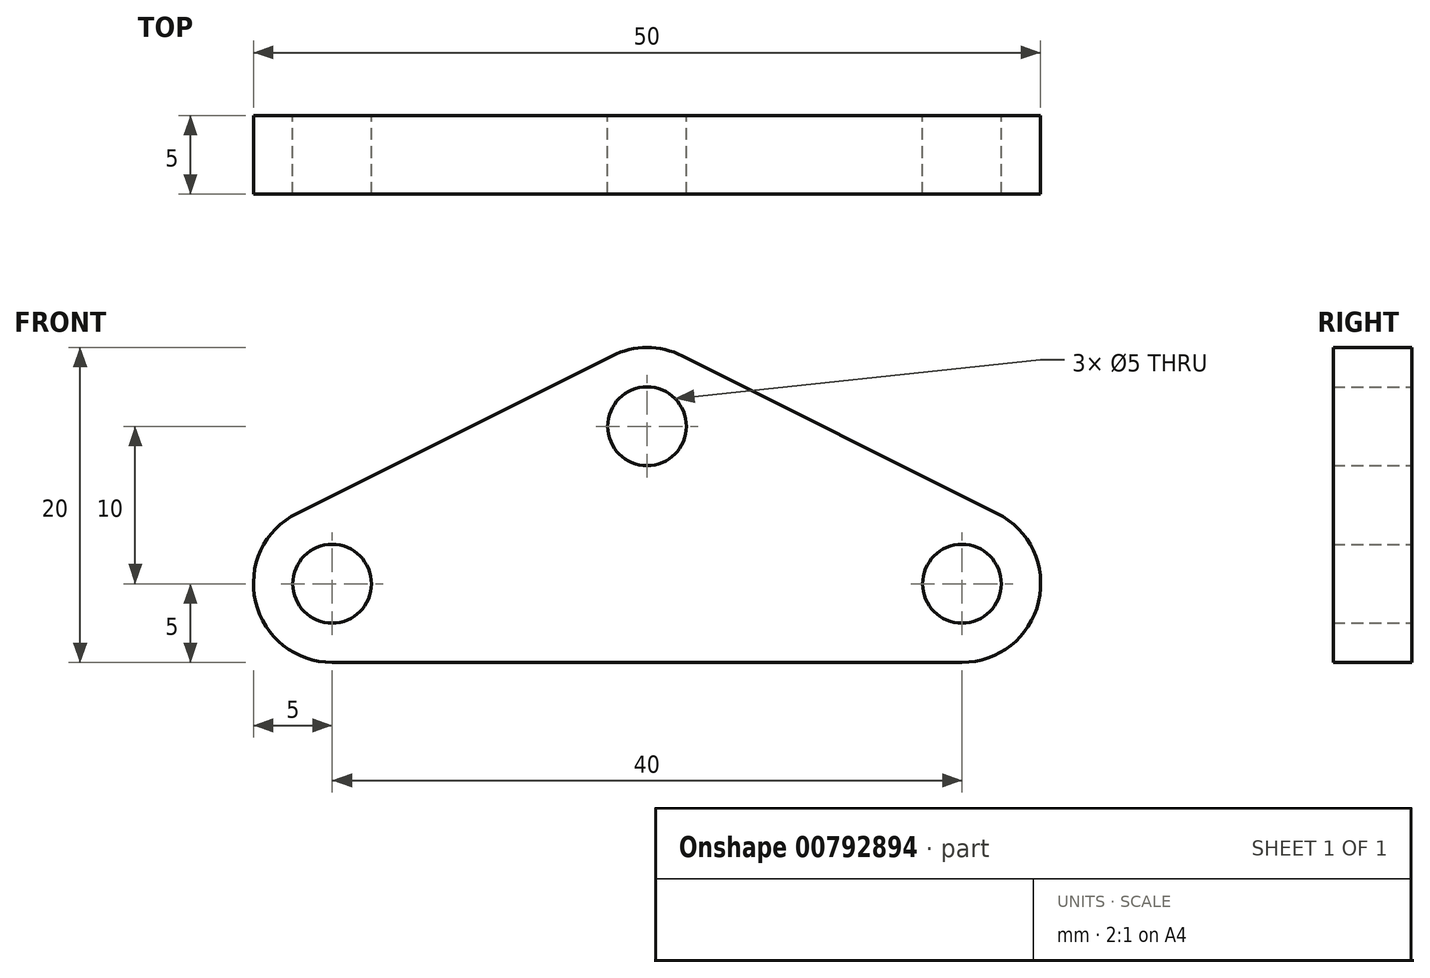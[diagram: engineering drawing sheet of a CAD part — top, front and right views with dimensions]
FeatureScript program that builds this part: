
annotation { "Feature Type Name" : "Feature", "Feature Type Description" : "" }
export const myFeature = defineFeature(function(context is Context, id is Id, definition is map)
    precondition{}
    {
        {
            var Q0;
            Q0=qCreatedBy(makeId("Front.planeOp"),FACE);
            var sketch = newSketch(context, id + "F0", { "sketchPlane" : qUnion([Q0])});
            skCircle(sketch, "E0", {"center": v(-20, 0) * mm, "radius": 2.5 * mm});
            skCircle(sketch, "E1", {"center": v(20, 0) * mm, "radius": 2.5 * mm});
            skCircle(sketch, "E2", {"center": v(0, 10) * mm, "radius": 2.5 * mm});
            skLineSegment(sketch, "E3", {"start": v(0, 0) * mm, "end": v(0, 10) * mm, "construction": true});
            skArc(sketch, "E4", {"start": v(-22.24, 4.47) * mm, "mid": v(-24.87, -1.15) * mm, "end": v(-20, -5) * mm});
            skArc(sketch, "E5", {"start": v(20, -5) * mm, "mid": v(24.87, -1.15) * mm, "end": v(22.24, 4.47) * mm});
            skArc(sketch, "E6", {"start": v(2.24, 14.47) * mm, "mid": v(0, 15) * mm, "end": v(-2.24, 14.47) * mm});
            skLineSegment(sketch, "E7", {"start": v(-20, -5) * mm, "end": v(20, -5) * mm});
            skLineSegment(sketch, "E8", {"start": v(-22.24, 4.47) * mm, "end": v(-2.24, 14.47) * mm});
            skLineSegment(sketch, "E9", {"start": v(2.24, 14.47) * mm, "end": v(22.24, 4.47) * mm});
            skSolve(sketch);
        }
        {
            var Q0;
            Q0=makeQuery(id+"F0.imprint","IMPRINT",FACE,{"disambiguationData":[TD([[makeQuery(id+"F0.imprint","IMPRINT",EDGE,{"derivedFrom":sQuery(id+"F0.wireOp",EDGE,"E0")}),-1.0]])]});
            extrude(context, id + "F1", {"entities" : qUnion([Q0]), "depth" : 5 * mm, "offsetDistance" : 25 * mm});
        }
    });
